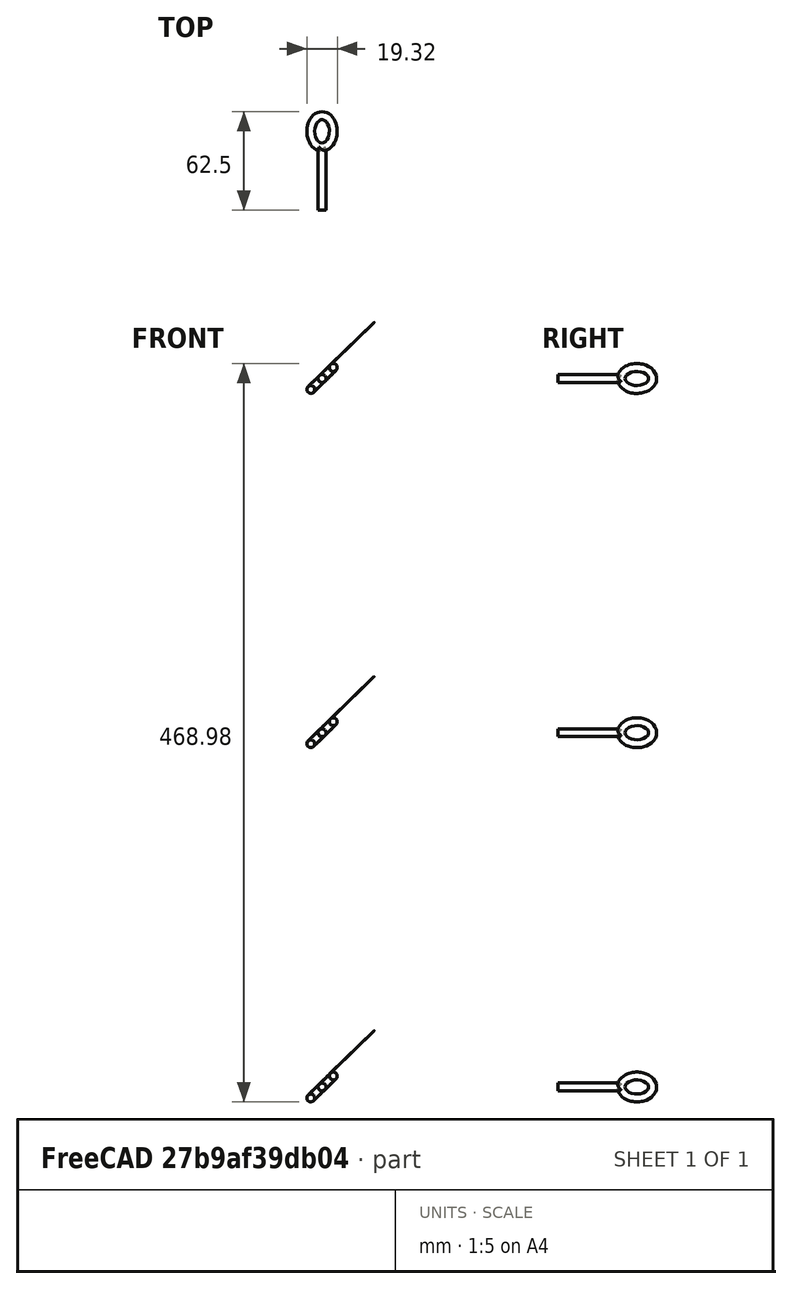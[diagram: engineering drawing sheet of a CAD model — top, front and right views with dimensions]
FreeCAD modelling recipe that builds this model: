
FCSTD DOCUMENT  (FreeCAD 0.17R10993 (Git))
Label: railing_eyelet
License: All rights reserved
LicenseURL: http://en.wikipedia.org/wiki/All_rights_reserved
objects: Part::Torus×1, Part::Cylinder×1, Part::MultiFuse×1, Part::FeaturePython×1
note: 4 computed .brp shape members not serialized (recipe doc carries the construction recipe); baked Part::Feature solids carry a one-line shape summary decoded from their .brp

FEATURE [Part::Torus] Torus
  Angle1 = -180
  Angle2 = 180
  Angle3 = 360
  AttacherType = Attacher::AttachEngine3D
  Placement = pos=(0,0,0) rot=(1,0,0;1.5708rad)
  Radius1 = 10
  Radius2 = 2.5
FEATURE [Part::Cylinder] Cylinder
  Angle = 360
  AttacherType = Attacher::AttachEngine3D
  Height = 40
  Placement = pos=(10,0,0) rot=(0,1,0;1.5708rad)
  Radius = 2.5
FEATURE [Part::MultiFuse] Fusion
  Placement = pos=(89.3902,-365.3,545) rot=(-0.677676,0.677677,0.285498;3.69779rad)
  Shapes = -> [Cylinder,Torus]
FEATURE [Part::FeaturePython] Array004  label="railing_eyelet"  # Draft array (typed FeaturePython)
  Angle = 360
  ArrayType = 0
  Axis = (0,0,1)
  Base = -> Fusion
  Center = (0,0,0)
  Fuse = false
  IntervalAxis = (0,0,0)
  IntervalX = (0,0,225)
  IntervalY = (630,0,615)
  IntervalZ = (0,0,0)
  NumberPolar = 1
  NumberX = 3
  NumberY = 1
  NumberZ = 1
